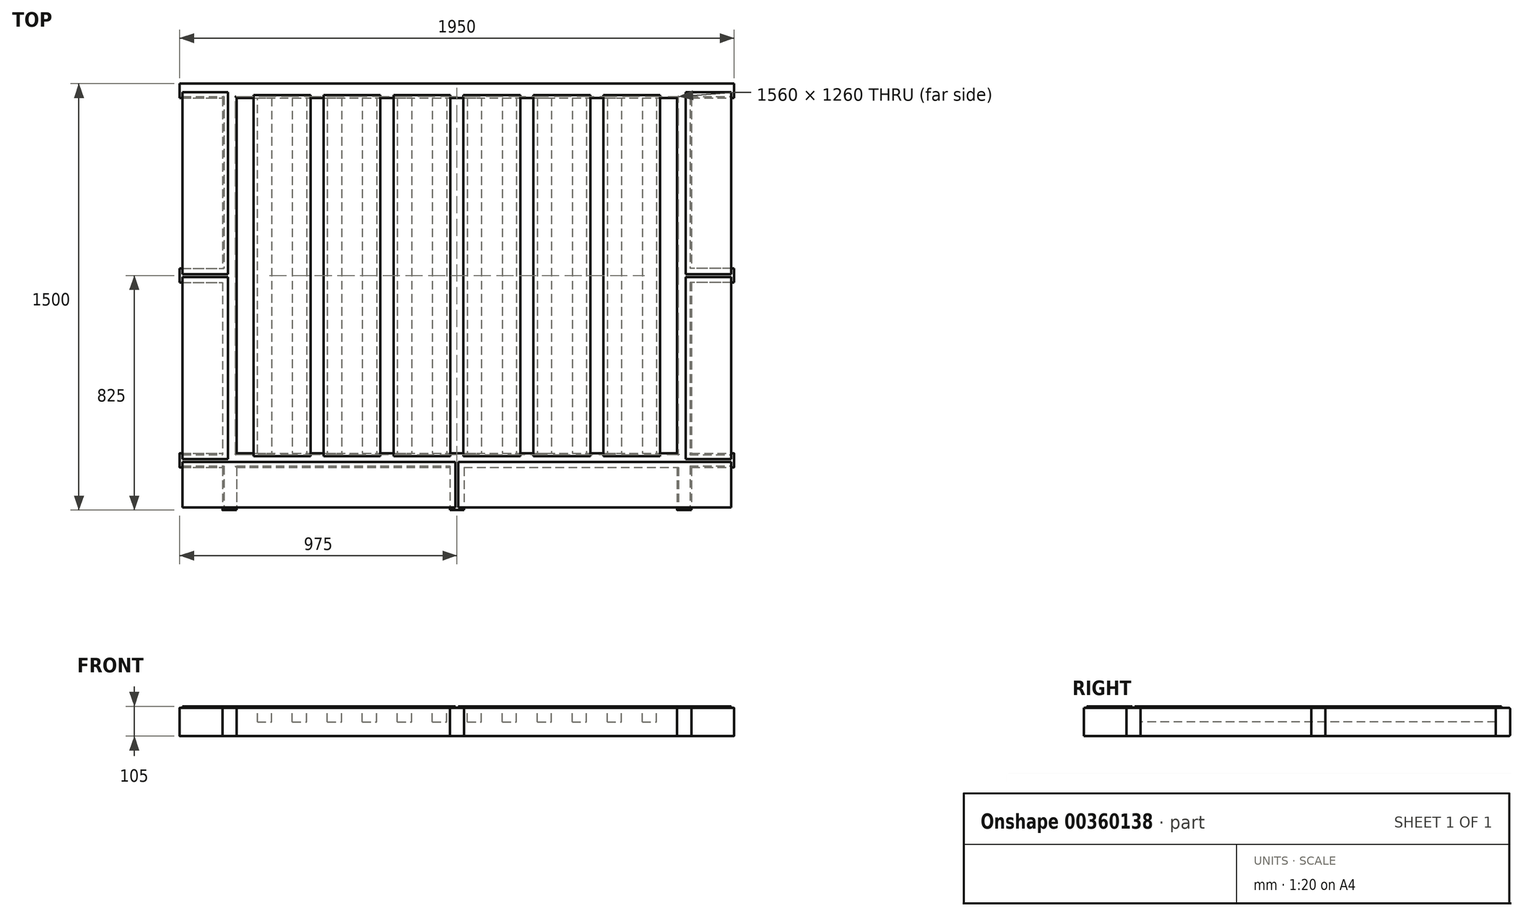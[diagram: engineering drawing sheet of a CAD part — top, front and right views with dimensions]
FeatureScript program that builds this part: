
annotation { "Feature Type Name" : "Feature", "Feature Type Description" : "" }
export const myFeature = defineFeature(function(context is Context, id is Id, definition is map)
    precondition{}
    {
        {
            var Q0;
            Q0=qCreatedBy(makeId("Top.planeOp"),FACE);
            var sketch = newSketch(context, id + "F0", { "sketchPlane" : qUnion([Q0])});
            skLineSegment(sketch, "E0.bottom", {"start": v(0, 0) * mm, "end": v(150, 0) * mm});
            skLineSegment(sketch, "E0.top", {"start": v(0, 50) * mm, "end": v(150, 50) * mm});
            skLineSegment(sketch, "E0.left", {"start": v(0, 0) * mm, "end": v(0, 50) * mm});
            skLineSegment(sketch, "E0.right", {"start": v(1950, 0) * mm, "end": v(1950, 50) * mm});
            skLineSegment(sketch, "E1.bottom", {"start": v(0, 1350) * mm, "end": v(1950, 1350) * mm});
            skLineSegment(sketch, "E1.left", {"start": v(0, 1350) * mm, "end": v(0, 1300) * mm});
            skLineSegment(sketch, "E1.right", {"start": v(1950, 1350) * mm, "end": v(1950, 1300) * mm});
            skLineSegment(sketch, "E2.trimOffspring", {"start": v(0, 1300) * mm, "end": v(150, 1300) * mm});
            skLineSegment(sketch, "E3.top", {"start": v(150, -150) * mm, "end": v(200, -150) * mm});
            skLineSegment(sketch, "E3.left", {"start": v(150, 1300) * mm, "end": v(150, 700) * mm});
            skLineSegment(sketch, "E3.right", {"start": v(200, 1300) * mm, "end": v(200, 50) * mm});
            skLineSegment(sketch, "E4.top", {"start": v(1750, -150) * mm, "end": v(1800, -150) * mm});
            skLineSegment(sketch, "E4.left", {"start": v(1750, 1300) * mm, "end": v(1750, 50) * mm});
            skLineSegment(sketch, "E4.right", {"start": v(1800, 1300) * mm, "end": v(1800, 50) * mm});
            skLineSegment(sketch, "E5.trimOffspring", {"start": v(1800, 0) * mm, "end": v(1950, 0) * mm});
            skLineSegment(sketch, "E6.trimOffspring", {"start": v(1800, 50) * mm, "end": v(1950, 50) * mm});
            skLineSegment(sketch, "E7.trimOffspring", {"start": v(1750, 0) * mm, "end": v(1750, -150) * mm});
            skLineSegment(sketch, "E8.trimOffspring", {"start": v(1800, 0) * mm, "end": v(1800, -150) * mm});
            skLineSegment(sketch, "E9.trimOffspring", {"start": v(1800, 1300) * mm, "end": v(1950, 1300) * mm});
            skLineSegment(sketch, "E10.trimOffspring", {"start": v(200, 1300) * mm, "end": v(1750, 1300) * mm});
            skLineSegment(sketch, "E11.trimOffspring", {"start": v(200, 50) * mm, "end": v(1750, 50) * mm});
            skLineSegment(sketch, "E12.trimOffspring", {"start": v(200, 0) * mm, "end": v(200, -150) * mm});
            skLineSegment(sketch, "E13.trimOffspring", {"start": v(150, 0) * mm, "end": v(150, -150) * mm});
            skLineSegment(sketch, "E14.trimOffspring", {"start": v(200, 0) * mm, "end": v(950, 0) * mm});
            skLineSegment(sketch, "E15.1.0.0", {"start": v(323.1, 1300) * mm, "end": v(323.1, 50) * mm});
            skLineSegment(sketch, "E15.2.0.0", {"start": v(446.2, 1300) * mm, "end": v(446.2, 50) * mm});
            skLineSegment(sketch, "E15.2.0.1", {"start": v(396.2, 1300) * mm, "end": v(396.2, 50) * mm});
            skLineSegment(sketch, "E15.3.0.0", {"start": v(569.3, 1300) * mm, "end": v(569.3, 50) * mm});
            skLineSegment(sketch, "E15.3.0.1", {"start": v(519.3, 1300) * mm, "end": v(519.3, 50) * mm});
            skLineSegment(sketch, "E15.4.0.0", {"start": v(692.4, 1300) * mm, "end": v(692.4, 50) * mm});
            skLineSegment(sketch, "E15.4.0.1", {"start": v(642.4, 1300) * mm, "end": v(642.4, 50) * mm});
            skLineSegment(sketch, "E15.5.0.0", {"start": v(815.5, 1300) * mm, "end": v(815.5, 50) * mm});
            skLineSegment(sketch, "E15.5.0.1", {"start": v(765.5, 1300) * mm, "end": v(765.5, 50) * mm});
            skLineSegment(sketch, "E15.6.0.0", {"start": v(938.6, 1300) * mm, "end": v(938.6, 50) * mm});
            skLineSegment(sketch, "E15.6.0.1", {"start": v(888.6, 1300) * mm, "end": v(888.6, 50) * mm});
            skLineSegment(sketch, "E15.7.0.0", {"start": v(1061.7, 1300) * mm, "end": v(1061.7, 50) * mm});
            skLineSegment(sketch, "E15.7.0.1", {"start": v(1011.7, 1300) * mm, "end": v(1011.7, 50) * mm});
            skLineSegment(sketch, "E15.8.0.0", {"start": v(1184.8, 1300) * mm, "end": v(1184.8, 50) * mm});
            skLineSegment(sketch, "E15.8.0.1", {"start": v(1134.8, 1300) * mm, "end": v(1134.8, 50) * mm});
            skLineSegment(sketch, "E15.9.0.0", {"start": v(1307.9, 1300) * mm, "end": v(1307.9, 50) * mm});
            skLineSegment(sketch, "E15.9.0.1", {"start": v(1257.9, 1300) * mm, "end": v(1257.9, 50) * mm});
            skLineSegment(sketch, "E15.10.0.0", {"start": v(1431, 1300) * mm, "end": v(1431, 50) * mm});
            skLineSegment(sketch, "E15.10.0.1", {"start": v(1381, 1300) * mm, "end": v(1381, 50) * mm});
            skLineSegment(sketch, "E15.11.0.0", {"start": v(1554.1, 1300) * mm, "end": v(1554.1, 50) * mm});
            skLineSegment(sketch, "E15.11.0.1", {"start": v(1504.1, 1300) * mm, "end": v(1504.1, 50) * mm});
            skLineSegment(sketch, "E15.12.0.0", {"start": v(1677.2, 1300) * mm, "end": v(1677.2, 50) * mm});
            skLineSegment(sketch, "E15.12.0.1", {"start": v(1627.2, 1300) * mm, "end": v(1627.2, 50) * mm});
            skLineSegment(sketch, "E15.direction1", {"start": v(150, 50) * mm, "end": v(273.1, 50) * mm, "construction": true});
            skLineSegment(sketch, "E16", {"start": v(273.1, 50) * mm, "end": v(273.1, 1300) * mm});
            skLineSegment(sketch, "E17.bottom", {"start": v(0, 700) * mm, "end": v(150, 700) * mm});
            skLineSegment(sketch, "E17.left", {"start": v(0, 700) * mm, "end": v(0, 675) * mm});
            skLineSegment(sketch, "E18", {"start": v(975, 1591.97) * mm, "end": v(975, -387.96) * mm, "construction": true});
            skPoint(sketch, "E18.startSnap0", {"position": v(975, 1350) * mm});
            skLineSegment(sketch, "E19.trimOffspring", {"start": v(150, 675) * mm, "end": v(2226.14, 675) * mm, "construction": true});
            skLineSegment(sketch, "E20.trimOffspring", {"start": v(150, 650) * mm, "end": v(150, 50) * mm});
            skLineSegment(sketch, "E21.MirrorCS", {"start": v(0, 650) * mm, "end": v(0, 675) * mm});
            skLineSegment(sketch, "E22.MirrorCS", {"start": v(0, 650) * mm, "end": v(150, 650) * mm});
            skLineSegment(sketch, "E23.MirrorCS", {"start": v(1950, 650) * mm, "end": v(1800, 650) * mm});
            skLineSegment(sketch, "E24.MirrorCS", {"start": v(1950, 700) * mm, "end": v(1950, 675) * mm});
            skLineSegment(sketch, "E25.MirrorCS", {"start": v(1950, 650) * mm, "end": v(1950, 675) * mm});
            skLineSegment(sketch, "E26.MirrorCS", {"start": v(1950, 700) * mm, "end": v(1800, 700) * mm});
            skLineSegment(sketch, "E27.top", {"start": v(950, -150) * mm, "end": v(1000, -150) * mm});
            skLineSegment(sketch, "E27.left", {"start": v(950, 0) * mm, "end": v(950, -150) * mm});
            skLineSegment(sketch, "E27.right", {"start": v(1000, 0) * mm, "end": v(1000, -150) * mm});
            skLineSegment(sketch, "E28.trimOffspring", {"start": v(1000, 0) * mm, "end": v(1750, 0) * mm});
            skSolve(sketch);
        }
        {
            var Q0;
            Q0 = qSketchRegion(id + "F0", true);
            extrude(context, id + "F1", {"entities" : qUnion([Q0]), "oppositeDirection" : true, "depth" : 100 * mm});
        }
        {
            var Q0;
            Q0=makeQuery(id+"FPwb0Jo6nws5QIE_0.opExtrude","CAP_EDGE",EDGE,{"disambiguationData":[OSD([sQuery(id+"F0.wireOp",EDGE,"E14.trimOffspring")])],"isStart":false});
            var Q1;
            Q1=makeQuery(id+"FPwb0Jo6nws5QIE_0.opExtrude","CAP_EDGE",EDGE,{"disambiguationData":[OSD([sQuery(id+"F0.wireOp",EDGE,"E7.trimOffspring")])],"isStart":false});
            var Q2;
            Q2=makeQuery(id+"FPwb0Jo6nws5QIE_0.opExtrude","CAP_EDGE",EDGE,{"disambiguationData":[OSD([sQuery(id+"F0.wireOp",EDGE,"E5.trimOffspring")])],"isStart":false});
            var Q3;
            Q3=makeQuery(id+"FPwb0Jo6nws5QIE_0.opExtrude","CAP_EDGE",EDGE,{"disambiguationData":[OSD([sQuery(id+"F0.wireOp",EDGE,"E8.trimOffspring")])],"isStart":false});
            var Q4;
            Q4=makeQuery(id+"FPwb0Jo6nws5QIE_0.opExtrude","CAP_EDGE",EDGE,{"disambiguationData":[OSD([sQuery(id+"F0.wireOp",EDGE,"E6.trimOffspring")])],"isStart":false});
            var Q5;
            Q5=makeQuery(id+"FPwb0Jo6nws5QIE_0.opExtrude","CAP_EDGE",EDGE,{"disambiguationData":[OSD([sQuery(id+"F0.wireOp",EDGE,"E4.right")])],"isStart":false});
            var Q6;
            Q6=makeQuery(id+"FPwb0Jo6nws5QIE_0.opExtrude","CAP_EDGE",EDGE,{"disambiguationData":[OSD([sQuery(id+"F0.wireOp",EDGE,"E4.left")])],"isStart":false});
            var Q7;
            Q7=makeQuery(id+"FPwb0Jo6nws5QIE_0.opExtrude","CAP_EDGE",EDGE,{"disambiguationData":[OSD([sQuery(id+"F0.wireOp",EDGE,"E11.trimOffspring")])],"isStart":false});
            var Q8;
            Q8=makeQuery(id+"FPwb0Jo6nws5QIE_0.opExtrude","CAP_EDGE",EDGE,{"disambiguationData":[OSD([sQuery(id+"F0.wireOp",EDGE,"E10.trimOffspring")])],"isStart":false});
            var Q9;
            Q9=makeQuery(id+"FPwb0Jo6nws5QIE_0.opExtrude","CAP_EDGE",EDGE,{"disambiguationData":[OSD([sQuery(id+"F0.wireOp",EDGE,"E1.bottom")])],"isStart":false});
            var Q10;
            Q10=makeQuery(id+"FPwb0Jo6nws5QIE_0.opExtrude","CAP_EDGE",EDGE,{"disambiguationData":[OSD([sQuery(id+"F0.wireOp",EDGE,"E9.trimOffspring")])],"isStart":false});
            var Q11;
            Q11=makeQuery(id+"FPwb0Jo6nws5QIE_0.opExtrude","CAP_EDGE",EDGE,{"disambiguationData":[OSD([sQuery(id+"F0.wireOp",EDGE,"E3.right")])],"isStart":false});
            var Q12;
            Q12=makeQuery(id+"FPwb0Jo6nws5QIE_0.opExtrude","CAP_EDGE",EDGE,{"disambiguationData":[OSD([sQuery(id+"F0.wireOp",EDGE,"E2.trimOffspring")])],"isStart":false});
            var Q13;
            Q13=makeQuery(id+"FPwb0Jo6nws5QIE_0.opExtrude","CAP_EDGE",EDGE,{"disambiguationData":[OSD([sQuery(id+"F0.wireOp",EDGE,"E3.left")])],"isStart":false});
            var Q14;
            Q14=makeQuery(id+"FPwb0Jo6nws5QIE_0.opExtrude","CAP_EDGE",EDGE,{"disambiguationData":[OSD([sQuery(id+"F0.wireOp",EDGE,"E0.top")])],"isStart":false});
            var Q15;
            Q15=makeQuery(id+"FPwb0Jo6nws5QIE_0.opExtrude","CAP_EDGE",EDGE,{"disambiguationData":[OSD([sQuery(id+"F0.wireOp",EDGE,"E0.bottom")])],"isStart":false});
            var Q16;
            Q16=makeQuery(id+"FPwb0Jo6nws5QIE_0.opExtrude","CAP_EDGE",EDGE,{"disambiguationData":[OSD([sQuery(id+"F0.wireOp",EDGE,"E13.trimOffspring")])],"isStart":false});
            var Q17;
            Q17=makeQuery(id+"FPwb0Jo6nws5QIE_0.opExtrude","CAP_EDGE",EDGE,{"disambiguationData":[OSD([sQuery(id+"F0.wireOp",EDGE,"E12.trimOffspring")])],"isStart":false});
            var Q18;
            Q18=makeQuery(id+"F1.opExtrude","CAP_EDGE",EDGE,{"disambiguationData":[OSD([sQuery(id+"F0.wireOp",EDGE,"E2.trimOffspring")])],"isStart":true});
            var Q19;
            Q19=makeQuery(id+"F1.opExtrude","CAP_EDGE",EDGE,{"disambiguationData":[OSD([sQuery(id+"F0.wireOp",EDGE,"E1.bottom")])],"isStart":true});
            var Q20;
            Q20=makeQuery(id+"F1.opExtrude","CAP_EDGE",EDGE,{"disambiguationData":[OSD([sQuery(id+"F0.wireOp",EDGE,"E10.trimOffspring")])],"isStart":true});
            var Q21;
            Q21=makeQuery(id+"F1.opExtrude","CAP_EDGE",EDGE,{"disambiguationData":[OSD([sQuery(id+"F0.wireOp",EDGE,"E3.right")])],"isStart":true});
            var Q22;
            Q22=makeQuery(id+"F1.opExtrude","CAP_EDGE",EDGE,{"disambiguationData":[OSD([sQuery(id+"F0.wireOp",EDGE,"E3.left")])],"isStart":true});
            var Q23;
            Q23=makeQuery(id+"F1.opExtrude","CAP_EDGE",EDGE,{"disambiguationData":[OSD([sQuery(id+"F0.wireOp",EDGE,"E14.trimOffspring")])],"isStart":true});
            var Q24;
            Q24=makeQuery(id+"F1.opExtrude","CAP_EDGE",EDGE,{"disambiguationData":[OSD([sQuery(id+"F0.wireOp",EDGE,"E11.trimOffspring")])],"isStart":true});
            var Q25;
            Q25=makeQuery(id+"F1.opExtrude","CAP_EDGE",EDGE,{"disambiguationData":[OSD([sQuery(id+"F0.wireOp",EDGE,"E0.top")])],"isStart":true});
            var Q26;
            Q26=makeQuery(id+"F1.opExtrude","CAP_EDGE",EDGE,{"disambiguationData":[OSD([sQuery(id+"F0.wireOp",EDGE,"E0.bottom")])],"isStart":true});
            var Q27;
            Q27=makeQuery(id+"F1.opExtrude","CAP_EDGE",EDGE,{"disambiguationData":[OSD([sQuery(id+"F0.wireOp",EDGE,"E13.trimOffspring")])],"isStart":true});
            var Q28;
            Q28=makeQuery(id+"F1.opExtrude","CAP_EDGE",EDGE,{"disambiguationData":[OSD([sQuery(id+"F0.wireOp",EDGE,"E4.left")])],"isStart":true});
            var Q29;
            Q29=makeQuery(id+"F1.opExtrude","CAP_EDGE",EDGE,{"disambiguationData":[OSD([sQuery(id+"F0.wireOp",EDGE,"E4.right")])],"isStart":true});
            var Q30;
            Q30=makeQuery(id+"F1.opExtrude","CAP_EDGE",EDGE,{"disambiguationData":[OSD([sQuery(id+"F0.wireOp",EDGE,"E6.trimOffspring")])],"isStart":true});
            var Q31;
            Q31=makeQuery(id+"F1.opExtrude","CAP_EDGE",EDGE,{"disambiguationData":[OSD([sQuery(id+"F0.wireOp",EDGE,"E5.trimOffspring")])],"isStart":true});
            var Q32;
            Q32=makeQuery(id+"F1.opExtrude","CAP_EDGE",EDGE,{"disambiguationData":[OSD([sQuery(id+"F0.wireOp",EDGE,"E8.trimOffspring")])],"isStart":true});
            var Q33;
            Q33=makeQuery(id+"F1.opExtrude","CAP_EDGE",EDGE,{"disambiguationData":[OSD([sQuery(id+"F0.wireOp",EDGE,"E7.trimOffspring")])],"isStart":true});
            var Q34;
            Q34=makeQuery(id+"F1.opExtrude","CAP_EDGE",EDGE,{"disambiguationData":[OSD([sQuery(id+"F0.wireOp",EDGE,"E9.trimOffspring")])],"isStart":true});
            fillet(context, id + "F2", {"entities" : qUnion([Q0, Q1, Q2, Q3, Q4, Q5, Q6, Q7, Q8, Q9, Q10, Q11, Q12, Q13, Q14, Q15, Q16, Q17, Q18, Q19, Q20, Q21, Q22, Q23, Q24, Q25, Q26, Q27, Q28, Q29, Q30, Q31, Q32, Q33, Q34]), "radius" : 5 * mm, "tangentPropagation" : true, "allowEdgeOverflow" : false});
        }
        {
            var Q0;
            {var subQ0=sQuery(id+"F0.wireOp",EDGE,"E15.1.0.0");Q0=makeQuery(id+"F0.imprint","IMPRINT",FACE,{"disambiguationData":[TD([[makeQuery(id+"F0.imprint","IMPRINT",EDGE,{"derivedFrom":subQ0}),-1.0]])]});}
            var Q1;
            {var subQ0=sQuery(id+"F0.wireOp",EDGE,"E15.2.0.0");Q1=makeQuery(id+"F0.imprint","IMPRINT",FACE,{"disambiguationData":[TD([[makeQuery(id+"F0.imprint","IMPRINT",EDGE,{"derivedFrom":subQ0}),-1.0]])]});}
            var Q2;
            {var subQ0=sQuery(id+"F0.wireOp",EDGE,"E15.3.0.0");Q2=makeQuery(id+"F0.imprint","IMPRINT",FACE,{"disambiguationData":[TD([[makeQuery(id+"F0.imprint","IMPRINT",EDGE,{"derivedFrom":subQ0}),-1.0]])]});}
            var Q3;
            {var subQ0=sQuery(id+"F0.wireOp",EDGE,"E15.4.0.0");Q3=makeQuery(id+"F0.imprint","IMPRINT",FACE,{"disambiguationData":[TD([[makeQuery(id+"F0.imprint","IMPRINT",EDGE,{"derivedFrom":subQ0}),-1.0]])]});}
            var Q4;
            {var subQ0=sQuery(id+"F0.wireOp",EDGE,"E15.5.0.0");Q4=makeQuery(id+"F0.imprint","IMPRINT",FACE,{"disambiguationData":[TD([[makeQuery(id+"F0.imprint","IMPRINT",EDGE,{"derivedFrom":subQ0}),-1.0]])]});}
            var Q5;
            {var subQ0=sQuery(id+"F0.wireOp",EDGE,"E15.6.0.0");Q5=makeQuery(id+"F0.imprint","IMPRINT",FACE,{"disambiguationData":[TD([[makeQuery(id+"F0.imprint","IMPRINT",EDGE,{"derivedFrom":subQ0}),-1.0]])]});}
            var Q6;
            {var subQ0=sQuery(id+"F0.wireOp",EDGE,"E15.7.0.0");Q6=makeQuery(id+"F0.imprint","IMPRINT",FACE,{"disambiguationData":[TD([[makeQuery(id+"F0.imprint","IMPRINT",EDGE,{"derivedFrom":subQ0}),-1.0]])]});}
            var Q7;
            {var subQ0=sQuery(id+"F0.wireOp",EDGE,"E15.8.0.0");Q7=makeQuery(id+"F0.imprint","IMPRINT",FACE,{"disambiguationData":[TD([[makeQuery(id+"F0.imprint","IMPRINT",EDGE,{"derivedFrom":subQ0}),-1.0]])]});}
            var Q8;
            {var subQ0=sQuery(id+"F0.wireOp",EDGE,"E15.9.0.0");Q8=makeQuery(id+"F0.imprint","IMPRINT",FACE,{"disambiguationData":[TD([[makeQuery(id+"F0.imprint","IMPRINT",EDGE,{"derivedFrom":subQ0}),-1.0]])]});}
            var Q9;
            {var subQ0=sQuery(id+"F0.wireOp",EDGE,"E15.10.0.0");Q9=makeQuery(id+"F0.imprint","IMPRINT",FACE,{"disambiguationData":[TD([[makeQuery(id+"F0.imprint","IMPRINT",EDGE,{"derivedFrom":subQ0}),-1.0]])]});}
            var Q10;
            {var subQ0=sQuery(id+"F0.wireOp",EDGE,"E15.11.0.0");Q10=makeQuery(id+"F0.imprint","IMPRINT",FACE,{"disambiguationData":[TD([[makeQuery(id+"F0.imprint","IMPRINT",EDGE,{"derivedFrom":subQ0}),-1.0]])]});}
            var Q11;
            {var subQ0=sQuery(id+"F0.wireOp",EDGE,"E15.12.0.0");Q11=makeQuery(id+"F0.imprint","IMPRINT",FACE,{"disambiguationData":[TD([[makeQuery(id+"F0.imprint","IMPRINT",EDGE,{"derivedFrom":subQ0}),-1.0]])]});}
            extrude(context, id + "F3", {"entities" : qUnion([Q0, Q1, Q2, Q3, Q4, Q5, Q6, Q7, Q8, Q9, Q10, Q11]), "oppositeDirection" : true, "depth" : 50 * mm});
        }
        {
            var Q0;
            Q0=makeQuery(id+"F1.opExtrude","CAP_EDGE",EDGE,{"disambiguationData":[OSD([sQuery(id+"F0.wireOp",EDGE,"E6.trimOffspring")])],"isStart":false});
            var Q1;
            Q1=makeQuery(id+"F1.opExtrude","CAP_EDGE",EDGE,{"disambiguationData":[OSD([sQuery(id+"F0.wireOp",EDGE,"E11.trimOffspring")])],"isStart":false});
            var Q2;
            Q2=makeQuery(id+"F1.opExtrude","CAP_EDGE",EDGE,{"disambiguationData":[OSD([sQuery(id+"F0.wireOp",EDGE,"E4.left")])],"isStart":false});
            var Q3;
            Q3=makeQuery(id+"F1.opExtrude","CAP_EDGE",EDGE,{"disambiguationData":[OSD([sQuery(id+"F0.wireOp",EDGE,"E4.right")])],"isStart":false});
            var Q4;
            Q4=makeQuery(id+"F1.opExtrude","CAP_EDGE",EDGE,{"disambiguationData":[OSD([sQuery(id+"F0.wireOp",EDGE,"E8.trimOffspring")])],"isStart":false});
            var Q5;
            Q5=makeQuery(id+"F1.opExtrude","CAP_EDGE",EDGE,{"disambiguationData":[OSD([sQuery(id+"F0.wireOp",EDGE,"E7.trimOffspring")])],"isStart":false});
            var Q6;
            Q6=makeQuery(id+"F1.opExtrude","CAP_EDGE",EDGE,{"disambiguationData":[OSD([sQuery(id+"F0.wireOp",EDGE,"E5.trimOffspring")])],"isStart":false});
            var Q7;
            Q7=makeQuery(id+"F1.opExtrude","CAP_EDGE",EDGE,{"disambiguationData":[OSD([sQuery(id+"F0.wireOp",EDGE,"E14.trimOffspring")])],"isStart":false});
            var Q8;
            Q8=makeQuery(id+"F1.opExtrude","CAP_EDGE",EDGE,{"disambiguationData":[OSD([sQuery(id+"F0.wireOp",EDGE,"E12.trimOffspring")])],"isStart":false});
            var Q9;
            Q9=makeQuery(id+"F1.opExtrude","CAP_EDGE",EDGE,{"disambiguationData":[OSD([sQuery(id+"F0.wireOp",EDGE,"E3.left")])],"isStart":false});
            var Q10;
            Q10=makeQuery(id+"F1.opExtrude","CAP_EDGE",EDGE,{"disambiguationData":[OSD([sQuery(id+"F0.wireOp",EDGE,"E3.right")])],"isStart":false});
            var Q11;
            Q11=makeQuery(id+"F1.opExtrude","CAP_EDGE",EDGE,{"disambiguationData":[OSD([sQuery(id+"F0.wireOp",EDGE,"E0.top")])],"isStart":false});
            var Q12;
            Q12=makeQuery(id+"F1.opExtrude","CAP_EDGE",EDGE,{"disambiguationData":[OSD([sQuery(id+"F0.wireOp",EDGE,"E0.bottom")])],"isStart":false});
            var Q13;
            Q13=makeQuery(id+"F1.opExtrude","CAP_EDGE",EDGE,{"disambiguationData":[OSD([sQuery(id+"F0.wireOp",EDGE,"E13.trimOffspring")])],"isStart":false});
            var Q14;
            Q14=makeQuery(id+"F1.opExtrude","CAP_EDGE",EDGE,{"disambiguationData":[OSD([sQuery(id+"F0.wireOp",EDGE,"E2.trimOffspring")])],"isStart":false});
            var Q15;
            Q15=makeQuery(id+"F1.opExtrude","CAP_EDGE",EDGE,{"disambiguationData":[OSD([sQuery(id+"F0.wireOp",EDGE,"E1.bottom")])],"isStart":false});
            var Q16;
            Q16=makeQuery(id+"F1.opExtrude","CAP_EDGE",EDGE,{"disambiguationData":[OSD([sQuery(id+"F0.wireOp",EDGE,"E10.trimOffspring")])],"isStart":false});
            var Q17;
            Q17=makeQuery(id+"F1.opExtrude","CAP_EDGE",EDGE,{"disambiguationData":[OSD([sQuery(id+"F0.wireOp",EDGE,"E9.trimOffspring")])],"isStart":false});
            fillet(context, id + "F4", {"entities" : qUnion([Q0, Q1, Q2, Q3, Q4, Q5, Q6, Q7, Q8, Q9, Q10, Q11, Q12, Q13, Q14, Q15, Q16, Q17]), "radius" : 5 * mm, "tangentPropagation" : true, "allowEdgeOverflow" : false});
        }
        {
            var Q0;
            Q0=qCreatedBy(makeId("Top.planeOp"),FACE);
            var sketch = newSketch(context, id + "F5", { "sketchPlane" : qUnion([Q0])});
            skLineSegment(sketch, "E29.bottom", {"start": v(1940, -140) * mm, "end": v(980, -140) * mm});
            skLineSegment(sketch, "E29.top", {"start": v(1940, 20) * mm, "end": v(980, 20) * mm});
            skLineSegment(sketch, "E29.left", {"start": v(1940, -140) * mm, "end": v(1940, 20) * mm});
            skLineSegment(sketch, "E29.right", {"start": v(10, -140) * mm, "end": v(10, 20) * mm});
            skLineSegment(sketch, "E30.bottom", {"start": v(10, 1320) * mm, "end": v(170, 1320) * mm});
            skLineSegment(sketch, "E30.top", {"start": v(10, 30) * mm, "end": v(170, 30) * mm});
            skLineSegment(sketch, "E30.left", {"start": v(10, 1320) * mm, "end": v(10, 680) * mm});
            skLineSegment(sketch, "E30.right", {"start": v(170, 1320) * mm, "end": v(170, 680) * mm});
            skLineSegment(sketch, "E31.bottom", {"start": v(1940, 30) * mm, "end": v(1780, 30) * mm});
            skLineSegment(sketch, "E31.top", {"start": v(1940, 1320) * mm, "end": v(1780, 1320) * mm});
            skLineSegment(sketch, "E31.left", {"start": v(1940, 30) * mm, "end": v(1940, 670) * mm});
            skLineSegment(sketch, "E31.right", {"start": v(1780, 30) * mm, "end": v(1780, 670) * mm});
            skLineSegment(sketch, "E32.bottom", {"start": v(1780, 680) * mm, "end": v(1940, 680) * mm});
            skLineSegment(sketch, "E32.top", {"start": v(1780, 670) * mm, "end": v(1940, 670) * mm});
            skLineSegment(sketch, "E33.trimOffspring", {"start": v(1940, 680) * mm, "end": v(1940, 1320) * mm});
            skLineSegment(sketch, "E34.trimOffspring", {"start": v(1780, 680) * mm, "end": v(1780, 1320) * mm});
            skLineSegment(sketch, "E35.bottom", {"start": v(10, 670) * mm, "end": v(170, 670) * mm});
            skLineSegment(sketch, "E35.top", {"start": v(10, 680) * mm, "end": v(170, 680) * mm});
            skLineSegment(sketch, "E36.trimOffspring", {"start": v(170, 670) * mm, "end": v(170, 30) * mm});
            skLineSegment(sketch, "E37.trimOffspring", {"start": v(10, 670) * mm, "end": v(10, 30) * mm});
            skLineSegment(sketch, "E38.left", {"start": v(970, 20) * mm, "end": v(970, -140) * mm});
            skLineSegment(sketch, "E38.right", {"start": v(980, 20) * mm, "end": v(980, -140) * mm});
            skLineSegment(sketch, "E39.trimOffspring", {"start": v(970, 20) * mm, "end": v(10, 20) * mm});
            skLineSegment(sketch, "E40.trimOffspring", {"start": v(970, -140) * mm, "end": v(10, -140) * mm});
            skSolve(sketch);
        }
        {
            var Q0;
            Q0 = qSketchRegion(id + "F5", true);
            extrude(context, id + "F6", {"entities" : qUnion([Q0]), "operationType" : NewBodyOperationType.ADD, "depth" : 5 * mm});
        }
        {
            var Q0;
            Q0=qCreatedBy(makeId("Top.planeOp"),FACE);
            var sketch = newSketch(context, id + "F7", { "sketchPlane" : qUnion([Q0])});
            skLineSegment(sketch, "E41.bottom", {"start": v(260, 1310) * mm, "end": v(460, 1310) * mm});
            skLineSegment(sketch, "E41.top", {"start": v(260, 40) * mm, "end": v(460, 40) * mm});
            skLineSegment(sketch, "E41.left", {"start": v(260, 1310) * mm, "end": v(260, 40) * mm});
            skLineSegment(sketch, "E41.right", {"start": v(460, 1310) * mm, "end": v(460, 40) * mm});
            skLineSegment(sketch, "E42.1.0.0", {"start": v(506, 1310) * mm, "end": v(506, 40) * mm});
            skLineSegment(sketch, "E42.1.0.1", {"start": v(506, 40) * mm, "end": v(706, 40) * mm});
            skLineSegment(sketch, "E42.1.0.2", {"start": v(706, 1310) * mm, "end": v(706, 40) * mm});
            skLineSegment(sketch, "E42.1.0.3", {"start": v(506, 1310) * mm, "end": v(706, 1310) * mm});
            skLineSegment(sketch, "E42.2.0.0", {"start": v(752, 1310) * mm, "end": v(752, 40) * mm});
            skLineSegment(sketch, "E42.2.0.1", {"start": v(752, 40) * mm, "end": v(952, 40) * mm});
            skLineSegment(sketch, "E42.2.0.2", {"start": v(952, 1310) * mm, "end": v(952, 40) * mm});
            skLineSegment(sketch, "E42.2.0.3", {"start": v(752, 1310) * mm, "end": v(952, 1310) * mm});
            skLineSegment(sketch, "E42.3.0.0", {"start": v(998, 1310) * mm, "end": v(998, 40) * mm});
            skLineSegment(sketch, "E42.3.0.1", {"start": v(998, 40) * mm, "end": v(1198, 40) * mm});
            skLineSegment(sketch, "E42.3.0.2", {"start": v(1198, 1310) * mm, "end": v(1198, 40) * mm});
            skLineSegment(sketch, "E42.3.0.3", {"start": v(998, 1310) * mm, "end": v(1198, 1310) * mm});
            skLineSegment(sketch, "E42.4.0.0", {"start": v(1244, 1310) * mm, "end": v(1244, 40) * mm});
            skLineSegment(sketch, "E42.4.0.1", {"start": v(1244, 40) * mm, "end": v(1444, 40) * mm});
            skLineSegment(sketch, "E42.4.0.2", {"start": v(1444, 1310) * mm, "end": v(1444, 40) * mm});
            skLineSegment(sketch, "E42.4.0.3", {"start": v(1244, 1310) * mm, "end": v(1444, 1310) * mm});
            skLineSegment(sketch, "E42.5.0.0", {"start": v(1490, 1310) * mm, "end": v(1490, 40) * mm});
            skLineSegment(sketch, "E42.5.0.1", {"start": v(1490, 40) * mm, "end": v(1690, 40) * mm});
            skLineSegment(sketch, "E42.5.0.2", {"start": v(1690, 1310) * mm, "end": v(1690, 40) * mm});
            skLineSegment(sketch, "E42.5.0.3", {"start": v(1490, 1310) * mm, "end": v(1690, 1310) * mm});
            skLineSegment(sketch, "E42.direction1", {"start": v(260, 40) * mm, "end": v(506, 40) * mm, "construction": true});
            skSolve(sketch);
        }
        {
            var Q0;
            Q0 = qSketchRegion(id + "F7", true);
            extrude(context, id + "F8", {"entities" : qUnion([Q0]), "depth" : 5 * mm});
        }
    });
